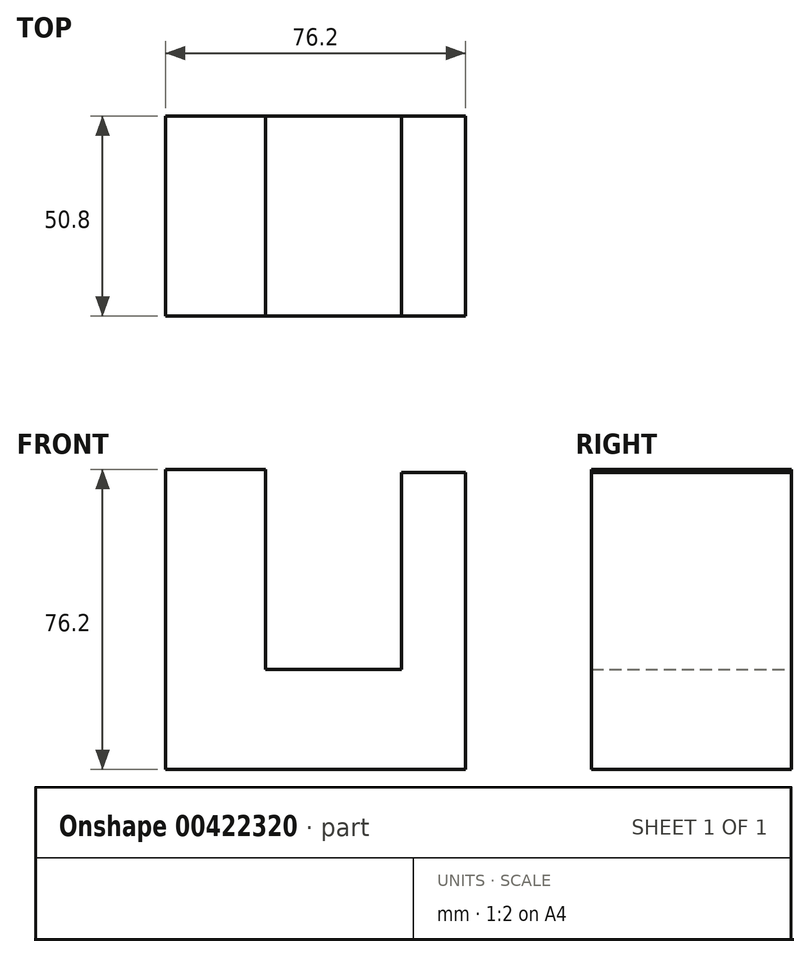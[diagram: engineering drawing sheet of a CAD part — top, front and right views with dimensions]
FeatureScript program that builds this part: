
annotation { "Feature Type Name" : "Feature", "Feature Type Description" : "" }
export const myFeature = defineFeature(function(context is Context, id is Id, definition is map)
    precondition{}
    {
        {
            var Q0;
            Q0=qCreatedBy(makeId("Front.planeOp"),FACE);
            var sketch = newSketch(context, id + "F0", { "sketchPlane" : qUnion([Q0])});
            skLineSegment(sketch, "E0", {"start": v(-58.03, 25.18) * mm, "end": v(-32.63, 25.18) * mm});
            skLineSegment(sketch, "E1", {"start": v(-58.03, 25.18) * mm, "end": v(-58.03, -51.02) * mm});
            skLineSegment(sketch, "E2", {"start": v(-58.03, -51.02) * mm, "end": v(18.17, -51.02) * mm});
            skLineSegment(sketch, "E3", {"start": v(18.17, -51.02) * mm, "end": v(18.17, 25.18) * mm});
            skLineSegment(sketch, "E4", {"start": v(-32.63, 25.18) * mm, "end": v(-32.63, -25.62) * mm});
            skLineSegment(sketch, "E5", {"start": v(-32.63, -25.62) * mm, "end": v(1.92, -25.62) * mm});
            skLineSegment(sketch, "E6", {"start": v(1.92, -25.62) * mm, "end": v(1.92, 24.49) * mm});
            skLineSegment(sketch, "E7", {"start": v(1.92, 24.49) * mm, "end": v(18.17, 24.49) * mm});
            skSolve(sketch);
        }
        {
            var Q0;
            Q0=makeQuery(id+"F0.imprint","IMPRINT",FACE,{"disambiguationData":[TD([[makeQuery(id+"F0.imprint","IMPRINT",EDGE,{"derivedFrom":sQuery(id+"F0.wireOp",EDGE,"E0")}),-1.0]])]});
            extrude(context, id + "F1", {"entities" : qUnion([Q0]), "depth" : 50.8 * mm});
        }
    });
